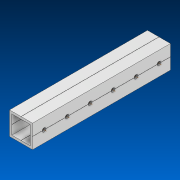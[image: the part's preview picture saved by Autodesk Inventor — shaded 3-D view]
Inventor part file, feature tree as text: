
AUTODESK INVENTOR PART (.ipt)
format: ipt  version: 2022.2 (Build 262287000, 287)  size: 645,632 bytes
history: native  units: in
note: dims shown in document units (in); Inventor stores cm internally (conversion verified against a paired STEP export)
features: other x6, extrude x1, pattern_linear x1, sketch x1, pattern_circular x1
ambient origin geometry x8: Origin, YZ Plane, XZ Plane, XY Plane, X Axis, Y Axis, Z Axis, Center Point
bodies: Solid1 (feature_tree)
feature tree (10):
  extrude  "Extrusion1"  Depth=1.0in
  other  "Work Axis1"
  pattern_linear  "Rectangular Pattern1"  Spacing1=0.0in  [1 undecoded]
  sketch  "Sketch1"  dims[d0=1.0in d1=53.0in d2=0.0in d3=2.3622in d5=1.0in]
  other  "Work Axis2"
  other  "Work Axis3"
  other  "Work Axis4"
  other  "Work Axis5"
  other  "Work Axis6"
  pattern_circular  "CirPattern2"
note: 1 required parameter value undecoded (feature->parameter linkage not recoverable at this tier; creation-order binding heuristic only, values carry confidence <= 0.55)
